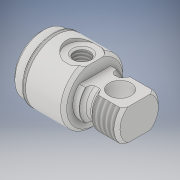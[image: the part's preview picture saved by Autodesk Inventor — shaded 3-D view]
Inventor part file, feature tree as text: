
AUTODESK INVENTOR PART (.ipt)
format: ipt  version: 2019 (Build 230136000, 136)  size: 344,576 bytes
history: native  units: in
note: dims shown in document units (in); Inventor stores cm internally (conversion verified against a paired STEP export)
features: other x168, sketch x8, revolve x5, thread x2, extrude x2, hole x1
ambient origin geometry x8: Origin, YZ Plane, XZ Plane, XY Plane, X Axis, Y Axis, Z Axis, Center Point
bodies: Solid1 (feature_tree)
feature tree (186):
  revolve  "Revolution1"  Angle=360.0deg
  revolve  "Revolution2"  [1 undecoded]
  thread  "Thread1"  [1 undecoded]
  extrude  "Extrusion1"  Depth=0.1736in TaperAngle=0.0deg
  hole  "Hole1"  [1 undecoded]
  revolve  "Revolution3"  [1 undecoded]
  revolve  "Revolution4"  [1 undecoded]
  thread  "Thread2"  [1 undecoded]
  revolve  "Revolution5"  [1 undecoded]
  extrude  "Extrusion2"  [1 undecoded]
  other  "1_XY"
  other  "1_YZ"
  other  "1_ZX"
  other  "1_X"
  other  "1_Y"
  other  "1_Z"
  other  "1_Center"
  other  "c1_XY"
  other  "c1_YZ"
  other  "c1_ZX"
  other  "c1_X"
  other  "c1_Y"
  other  "c1_Z"
  other  "c1_Center"
  other  "c2_XY"
  other  "c2_YZ"
  other  "c2_ZX"
  other  "c2_X"
  other  "c2_Y"
  other  "c2_Z"
  other  "c2_Center"
  other  "cc1_XY"
  other  "cc1_YZ"
  other  "cc1_ZX"
  other  "cc1_X"
  other  "cc1_Y"
  other  "cc1_Z"
  other  "cc1_Center"
  other  "cc2_XY"
  other  "cc2_YZ"
  other  "cc2_ZX"
  other  "cc2_X"
  other  "cc2_Y"
  other  "cc2_Z"
  other  "cc2_Center"
  other  "lovra1_XY"
  other  "lovra1_YZ"
  other  "lovra1_ZX"
  other  "lovra1_X"
  other  "lovra1_Y"
  other  "lovra1_Z"
  other  "lovra1_Center"
  other  "lovra2_XY"
  other  "lovra2_YZ"
  other  "lovra2_ZX"
  other  "lovra2_X"
  other  "lovra2_Y"
  other  "lovra2_Z"
  other  "lovra2_Center"
  other  "lovra21_XY"
  other  "lovra21_YZ"
  other  "lovra21_ZX"
  other  "lovra21_X"
  other  "lovra21_Y"
  other  "lovra21_Z"
  other  "lovra21_Center"
  other  "lovra22_XY"
  other  "lovra22_YZ"
  other  "lovra22_ZX"
  other  "lovra22_X"
  other  "lovra22_Y"
  other  "lovra22_Z"
  other  "lovra22_Center"
  other  "lovra3_XY"
  other  "lovra3_YZ"
  other  "lovra3_ZX"
  other  "lovra3_X"
  other  "lovra3_Y"
  other  "lovra3_Z"
  other  "lovra3_Center"
  other  "olen_XY"
  other  "olen_YZ"
  other  "olen_ZX"
  other  "olen_X"
  other  "olen_Y"
  other  "olen_Z"
  other  "olen_Center"
  other  "p1_XY"
  other  "p1_YZ"
  other  "p1_ZX"
  other  "p1_X"
  other  "p1_Y"
  other  "p1_Z"
  other  "p1_Center"
  other  "p2_XY"
  other  "p2_YZ"
  other  "p2_ZX"
  other  "p2_X"
  other  "p2_Y"
  other  "p2_Z"
  other  "p2_Center"
  other  "port_XY"
  other  "port_YZ"
  other  "port_ZX"
  other  "port_X"
  other  "port_Y"
  other  "port_Z"
  other  "port_Center"
  other  "port2_XY"
  other  "port2_YZ"
  other  "port2_ZX"
  other  "port2_X"
  other  "port2_Y"
  other  "port2_Z"
  other  "port2_Center"
  other  "thd1_XY"
  other  "thd1_YZ"
  other  "thd1_ZX"
  other  "thd1_X"
  other  "thd1_Y"
  other  "thd1_Z"
  other  "thd1_Center"
  other  "thd2_XY"
  other  "thd2_YZ"
  other  "thd2_ZX"
  other  "thd2_X"
  other  "thd2_Y"
  other  "thd2_Z"
  other  "thd2_Center"
  other  "to_mounting_bracket_XY"
  other  "to_mounting_bracket_YZ"
  other  "to_mounting_bracket_ZX"
  other  "to_mounting_bracket_X"
  other  "to_mounting_bracket_Y"
  other  "to_mounting_bracket_Z"
  other  "to_mounting_bracket_Center"
  other  "to_nut_XY"
  other  "to_nut_YZ"
  other  "to_nut_ZX"
  other  "to_nut_X"
  other  "to_nut_Y"
  other  "to_nut_Z"
  other  "to_nut_Center"
  other  "to_pin_XY"
  other  "to_pin_YZ"
  other  "to_pin_ZX"
  other  "to_pin_X"
  other  "to_pin_Y"
  other  "to_pin_Z"
  other  "to_pin_Center"
  other  "to_pin_1_XY"
  other  "to_pin_1_YZ"
  other  "to_pin_1_ZX"
  other  "to_pin_1_X"
  other  "to_pin_1_Y"
  other  "to_pin_1_Z"
  other  "to_pin_1_Center"
  other  "to_pin_r_XY"
  other  "to_pin_r_YZ"
  other  "to_pin_r_ZX"
  other  "to_pin_r_X"
  other  "to_pin_r_Y"
  other  "to_pin_r_Z"
  other  "to_pin_r_Center"
  other  "to_screw_XY"
  other  "to_screw_YZ"
  other  "to_screw_ZX"
  other  "to_screw_X"
  other  "to_screw_Y"
  other  "to_screw_Z"
  other  "to_screw_Center"
  other  "to_tube_XY"
  other  "to_tube_YZ"
  other  "to_tube_ZX"
  other  "to_tube_X"
  other  "to_tube_Y"
  other  "to_tube_Z"
  other  "to_tube_Center"
  sketch  "Sketch_18"  dims[d6=0.154in d7=0.75in d8=0.375in d9=0.25in d10=0.5635in d11=0.484in d12=120.0deg d13=360.0deg]
  sketch  "Sketch_15"  dims[d2=0.2157in d3=0.0in d4=0.437in d5=0.0in]
  sketch  "Sketch_70"
  sketch  "Sketch4"  dims[d0=360.0deg d1=360.0deg]
  sketch  "Sketch_45"  dims[d20=0.0in d21=0.0in d22=0.0in d23=0.0in d24=0.0in d25=0.0in d26=0.0in d27=0.0in d28=0.0in]
  sketch  "Sketch_46"
  sketch  "Sketch_24"  dims[d14=360.0deg d15=0.1736in d16=0.0in]
  sketch  "Sketch_43"  dims[d17=360.0deg d18=0.4605in d19=0.0in]
note: 8 required parameter values undecoded (feature->parameter linkage not recoverable at this tier; creation-order binding heuristic only, values carry confidence <= 0.55)